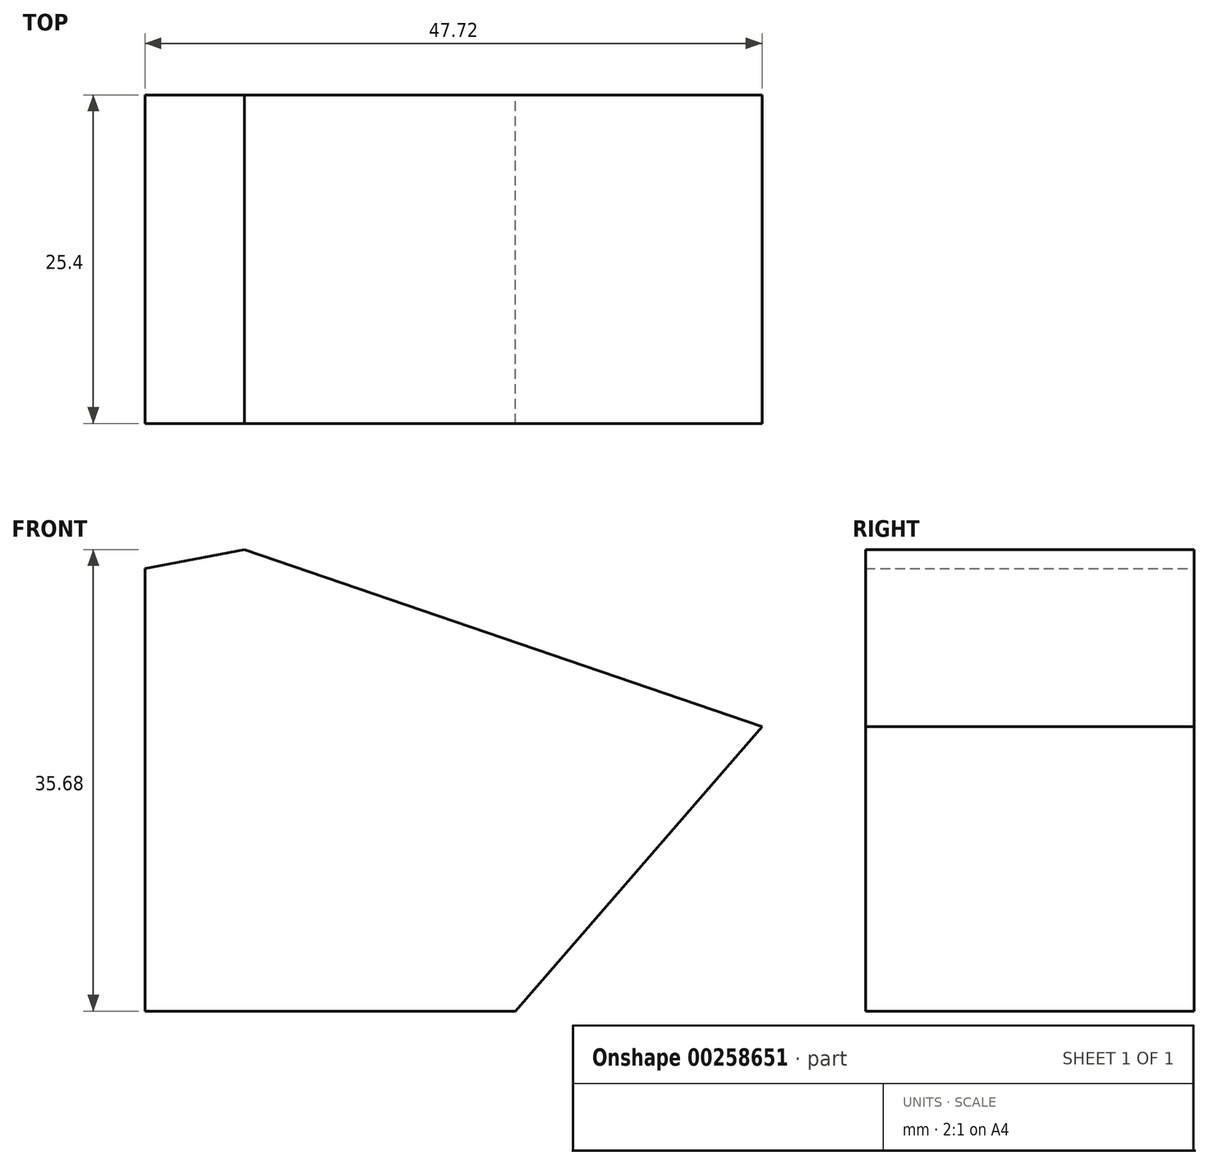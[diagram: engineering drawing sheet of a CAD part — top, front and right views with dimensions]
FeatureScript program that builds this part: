
annotation { "Feature Type Name" : "Feature", "Feature Type Description" : "" }
export const myFeature = defineFeature(function(context is Context, id is Id, definition is map)
    precondition{}
    {
        {
            var Q0;
            Q0=qCreatedBy(makeId("Front.planeOp"),FACE);
            var sketch = newSketch(context, id + "F0", { "sketchPlane" : qUnion([Q0])});
            skLineSegment(sketch, "E0", {"start": v(-20.95, 41.7) * mm, "end": v(19.09, 28) * mm});
            skLineSegment(sketch, "E1", {"start": v(19.09, 28) * mm, "end": v(0, 6.02) * mm});
            skLineSegment(sketch, "E2", {"start": v(0, 6.02) * mm, "end": v(-28.63, 6.02) * mm});
            skLineSegment(sketch, "E3", {"start": v(-28.63, 6.02) * mm, "end": v(-28.63, 40.25) * mm});
            skLineSegment(sketch, "E4", {"start": v(-28.63, 40.25) * mm, "end": v(-20.95, 41.7) * mm});
            skSolve(sketch);
        }
        {
            var Q0;
            Q0=makeQuery(id+"F0.imprint","IMPRINT",FACE,{"disambiguationData":[TD([[makeQuery(id+"F0.imprint","IMPRINT",EDGE,{"derivedFrom":sQuery(id+"F0.wireOp",EDGE,"E0")}),-1.0]])]});
            var Q1;
            Q1 = qSketchRegion(id + "F0", true);
            extrude(context, id + "F1", {"entities" : qUnion([Q0, Q1]), "depth" : 25.4 * mm});
        }
    });
